# Revit family: Smartline_START_2800mm
name_source: partatom
category: Mechanical Equipment
revit_build: Autodesk Revit 2018 (Build: 18.0.0.0)
units: mm (PartAtom-declared; Revit-internal decimal feet)

## family parameters
Always vertical = Yes
Classification = None
Cut with Voids When Loaded = No
Part Type = Normal
Room Calculation Point = No
Round Connector Dimension = Use Diameter
Shared = No

## types (2) — shared parameters
Abhänger_Abstand_VuH = 200 mm  [stored 0.656168 ft]
Abhänger_Länge = 741.5 mm
Abhänger_Mitte_Revsisionsraum = No
Abhänger_NichtProfil = Yes
Abhänger_Profil = No
Abhänger_ProfilTyp = No
Abhänger_Profil_Mitte = No
Abhänger_anzeigen = Yes
Abstand Anschlüsse Verbinder = 100 mm  [stored 0.328084 ft]
DSP_Druckverlust_viertel = 0.0 bar
Description = Heiz- und Kühlsegel
Durchmesser_Rücklauf = 15 mm
Durchmesser_Vorlauf = 15 mm
Dämmung = Yes
Enthält Luftauslässe = No
Enthält einen Volumenstromregler = Yes
Familien_Version = 0.1.10
Leergewicht = 22.00 kg
Manufacturer = FRENGER SYSTEMEN BV
Massenstrom (kg/h) = 19.486571
Model = Smartline
PB = 1000 mm  [stored 3.28084 ft]
PB_halbe = 500 mm  [stored 1.64042 ft]
PL = 2800 mm  [stored 9.18635 ft]
Plattenbreite = 1000 mm  [stored 3.28084 ft]
Plattenhöhe = 58.5 mm  [stored 0.191929 ft]
Plattenlänge = 2800 mm  [stored 9.18635 ft]
Randabstand Anschlüsse = 75 mm  [stored 0.246063 ft]
Raumtemperatur_Kühlen = 26 °C
Revisionsraum_anzeigen = No
Rücklauftemperatur_Kühlen = 19 °C
Temperaturdifferenz_Heizen = 20 °C
Temperaturdifferenz_Kühlen = -3 °C
URL = https://frenger.de
UT_Kühlen = 9 °C
Volumenabsorber_Einzel = No
Volumenabsorber_Hoehe = 80 mm  [stored 0.262467 ft]
Volumenabsorber_Offset = 25 mm  [stored 0.082021 ft]
Volumenstrom = 0.0 L/s
Vorlauftemperatur_Kühlen = 16 °C
Wasser_je_m = 1.00 kg/m
Wasserinhalt = 2.00 kg
ÜT_Heizen = 37 °C

## per-type parameters (varying)
| type | Abhänger_Anzahl | Abhänger_Mitte | DSP_Druckverlust_halbe | Druckverlust | Gewicht | Leergewicht_je_m | Leistung_Heizen | Leistung_Kühlen | Raumtemperatur_Heizen | Rücklauftemperatur_Heizen | Volumenabsorber | Volumenabsorber_Doppel | Vorlauftemperatur_Heizen |
| STANDARD | 2 | No | 0.1 bar | 0.2 bar | 24.00 kg | 11.00 kg/m | 295 W | 56 W | 23 °C | 50 °C | No | No | 70 °C |
| 008-START-1000mm | 3 | Yes | 0.0 bar | 0.0 bar | 76.44 kg | 24.70 kg/m | 473 W | 197 W | 20 °C | 35 °C | Yes | Yes | 40 °C |

note: [stored X ft] marks values corroborated as IEEE doubles in the binary element streams (Revit-internal decimal feet)
